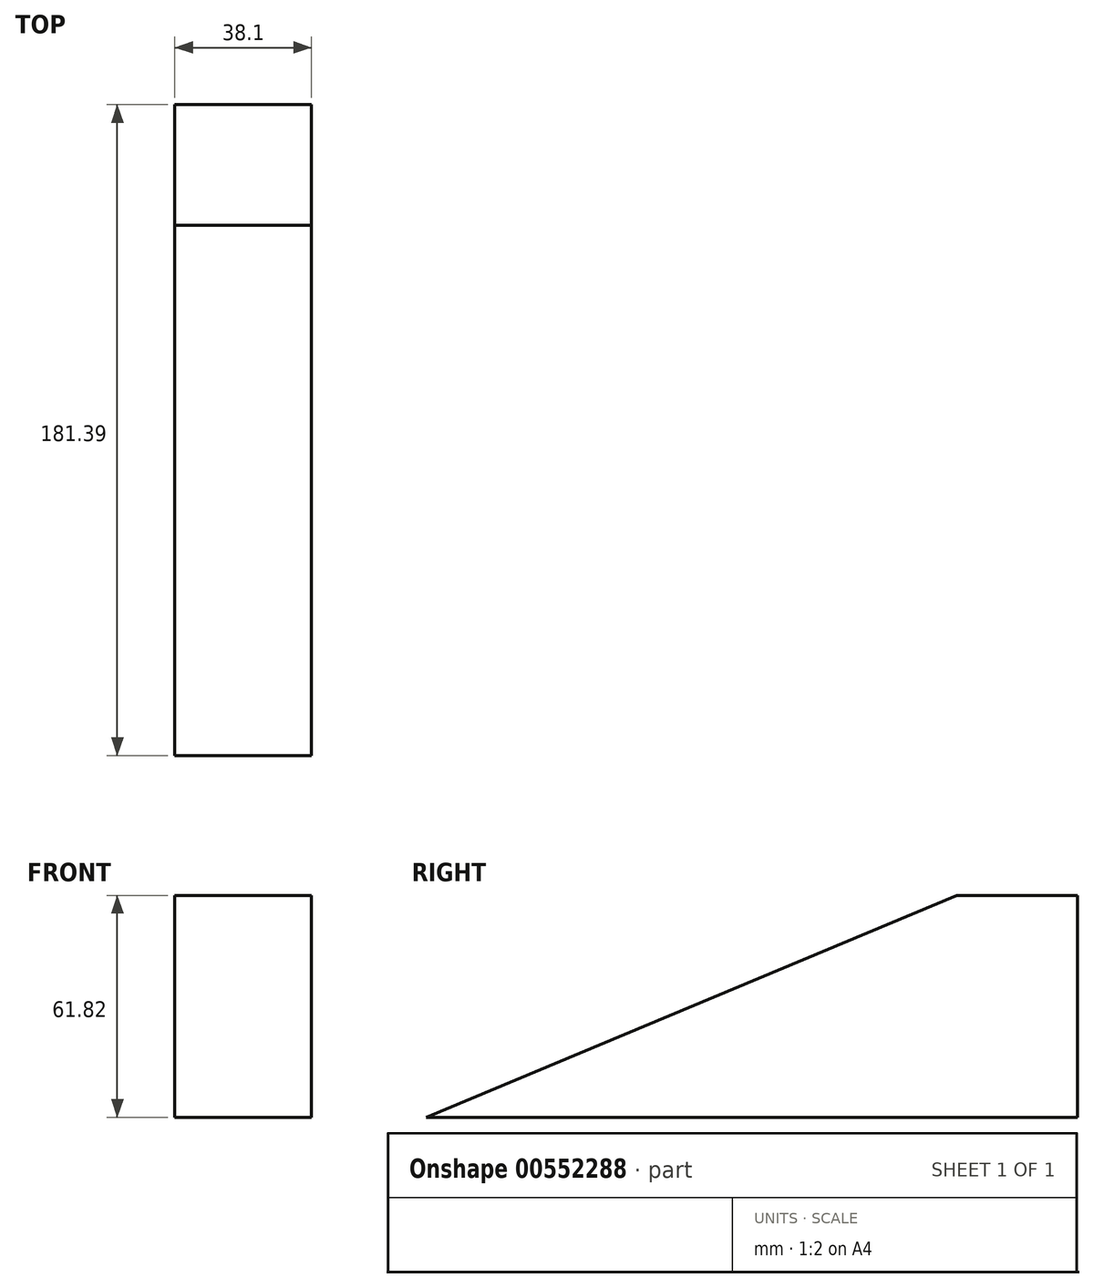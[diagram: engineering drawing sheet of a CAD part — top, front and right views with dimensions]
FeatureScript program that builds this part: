
annotation { "Feature Type Name" : "Feature", "Feature Type Description" : "" }
export const myFeature = defineFeature(function(context is Context, id is Id, definition is map)
    precondition{}
    {
        {
            var Q0;
            Q0=qCreatedBy(makeId("Right.planeOp"),FACE);
            var sketch = newSketch(context, id + "F0", { "sketchPlane" : qUnion([Q0])});
            skLineSegment(sketch, "E0", {"start": v(94.33, 16.4) * mm, "end": v(94.33, -45.41) * mm});
            skLineSegment(sketch, "E1", {"start": v(94.33, -45.41) * mm, "end": v(-87.06, -45.41) * mm});
            skLineSegment(sketch, "E2", {"start": v(94.33, 16.4) * mm, "end": v(60.75, 16.4) * mm});
            skLineSegment(sketch, "E3", {"start": v(60.75, 16.4) * mm, "end": v(-87.06, -45.41) * mm});
            skSolve(sketch);
        }
        {
            var Q0;
            Q0 = qSketchRegion(id + "F0", true);
            extrude(context, id + "F1", {"entities" : qUnion([Q0]), "depth" : 38.1 * mm, "offsetDistance" : 25.4 * mm});
        }
    });
